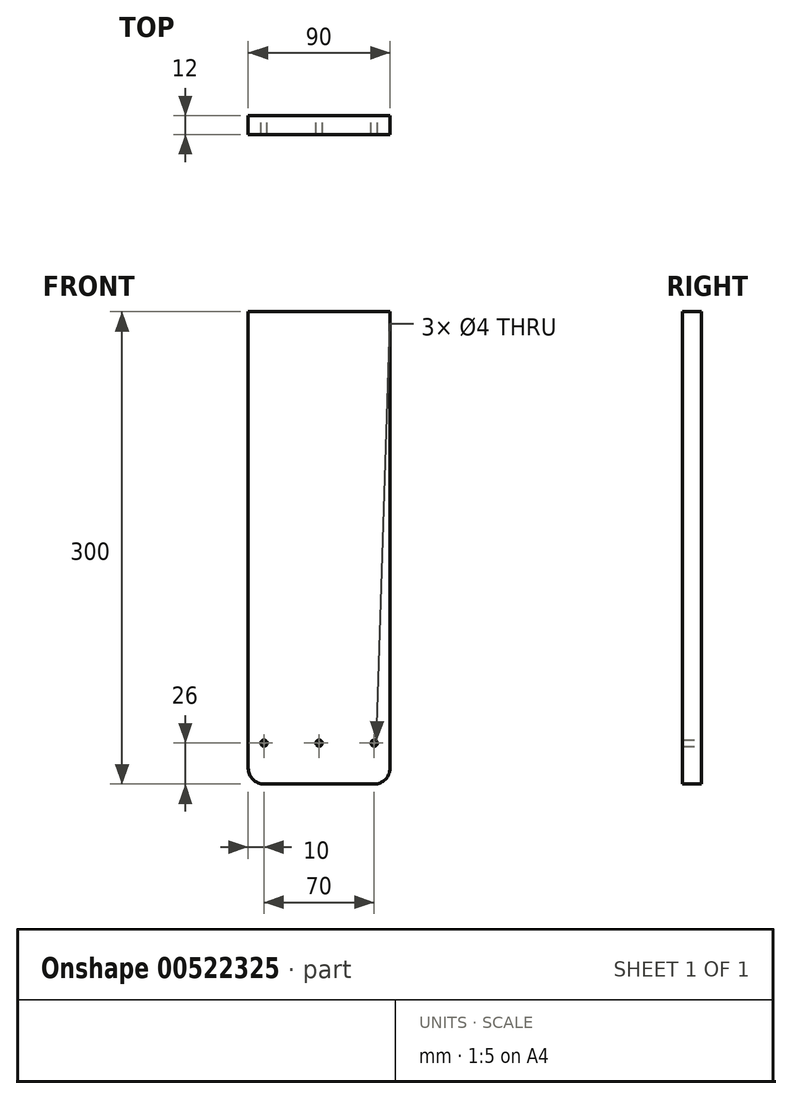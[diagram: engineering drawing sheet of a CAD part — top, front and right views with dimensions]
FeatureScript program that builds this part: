
annotation { "Feature Type Name" : "Feature", "Feature Type Description" : "" }
export const myFeature = defineFeature(function(context is Context, id is Id, definition is map)
    precondition{}
    {
        {
            var Q0;
            Q0=qCreatedBy(makeId("Front.planeOp"),FACE);
            var sketch = newSketch(context, id + "F0", { "sketchPlane" : qUnion([Q0])});
            skLineSegment(sketch, "E0.bottom", {"start": v(45, -150) * mm, "end": v(-45, -150) * mm});
            skLineSegment(sketch, "E0.top", {"start": v(45, 150) * mm, "end": v(-45, 150) * mm});
            skLineSegment(sketch, "E0.left", {"start": v(45, -150) * mm, "end": v(45, 150) * mm});
            skLineSegment(sketch, "E0.right", {"start": v(-45, -150) * mm, "end": v(-45, 150) * mm});
            skPoint(sketch, "E0.middle", {"position": v(0, 0) * mm});
            skLineSegment(sketch, "E1.bottom", {"start": v(-45, -130) * mm, "end": v(45, -130) * mm});
            skLineSegment(sketch, "E1.top", {"start": v(-45, -118) * mm, "end": v(45, -118) * mm});
            skLineSegment(sketch, "E1.left", {"start": v(-45, -130) * mm, "end": v(-45, -118) * mm});
            skLineSegment(sketch, "E1.right", {"start": v(45, -130) * mm, "end": v(45, -118) * mm});
            skLineSegment(sketch, "E2", {"start": v(-45, -124) * mm, "end": v(45, -124) * mm, "construction": true});
            skCircle(sketch, "E3", {"center": v(0, -124) * mm, "radius": 2 * mm});
            skCircle(sketch, "E4", {"center": v(35, -124) * mm, "radius": 2 * mm});
            skCircle(sketch, "E5", {"center": v(-35, -124) * mm, "radius": 2 * mm});
            skSolve(sketch);
        }
        {
            var Q0;
            Q0 = qSketchRegion(id + "F0", true);
            extrude(context, id + "F1", {"entities" : qUnion([Q0]), "depth" : 12 * mm, "offsetDistance" : 25 * mm});
        }
        {
            var Q0;
            Q0=makeQuery(id+"F1.opExtrude","SWEPT_EDGE",EDGE,{"disambiguationData":[OSD([sQuery(id+"F0.wireOp",EDGE,"E0.bottom"),sQuery(id+"F0.wireOp",EDGE,"E0.left")])]});
            var Q1;
            Q1=makeQuery(id+"F1.opExtrude","SWEPT_EDGE",EDGE,{"disambiguationData":[OSD([sQuery(id+"F0.wireOp",EDGE,"E0.bottom"),sQuery(id+"F0.wireOp",EDGE,"E0.right")])]});
            fillet(context, id + "F2", {"entities" : qUnion([Q0, Q1]), "radius" : 10 * mm, "tangentPropagation" : true, "allowEdgeOverflow" : false});
        }
    });
